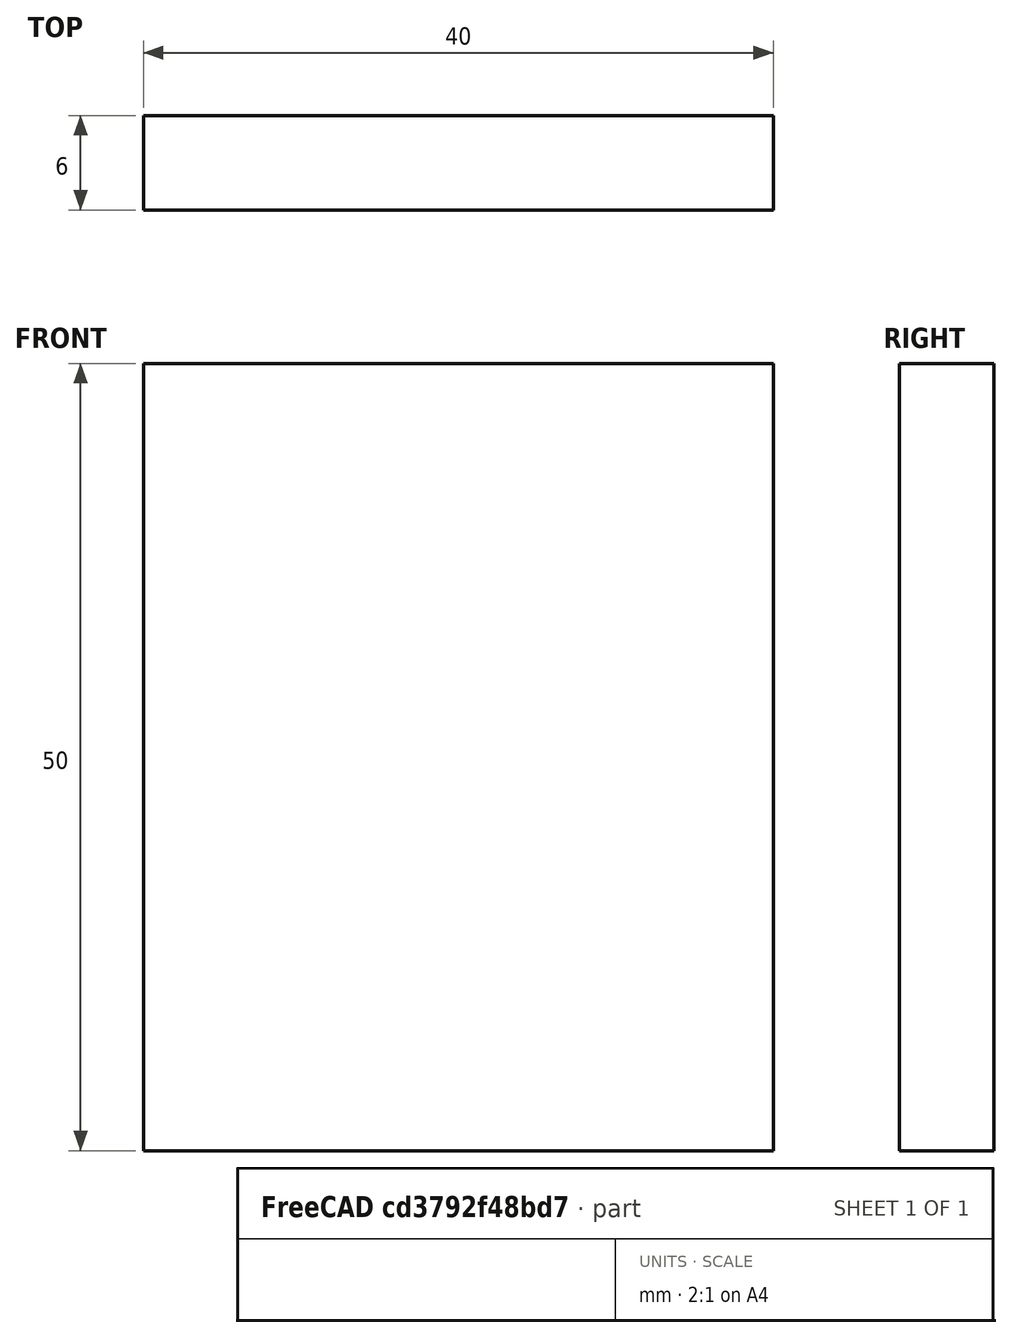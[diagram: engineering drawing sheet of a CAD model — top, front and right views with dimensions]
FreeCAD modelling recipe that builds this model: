
FCSTD DOCUMENT  (FreeCAD 0.15R4671 (Git))
Label: Flat Bar 40x6 EN10058 S235JR
License: All rights reserved
LicenseURL: http://en.wikipedia.org/wiki/All_rights_reserved
objects: Sketcher::SketchObject×1, Part::Extrusion×1
note: 2 computed .brp shape members not serialized (recipe doc carries the construction recipe); baked Part::Feature solids carry a one-line shape summary decoded from their .brp

FEATURE [Sketcher::SketchObject] Sketch
  sketch-geometry (4):
    g0: LineSegment StartX=-20 StartY=-3 StartZ=0 EndX=20 EndY=-3 EndZ=0
    g1: LineSegment StartX=20 StartY=-3 StartZ=0 EndX=20 EndY=3 EndZ=0
    g2: LineSegment StartX=20 StartY=3 StartZ=0 EndX=-20 EndY=3 EndZ=0
    g3: LineSegment StartX=-20 StartY=3 StartZ=0 EndX=-20 EndY=-3 EndZ=0
  constraints (12):
    c: Coincident(g0,g1)
    c: Coincident(g1,g2)
    c: Coincident(g2,g3)
    c: Coincident(g3,g0)
    c: Horizontal(g0)
    c: Horizontal(g2)
    c: Vertical(g1)
    c: Vertical(g3)
    c: Symmetric(g1,g2,g-2)
    c: Symmetric(g0,g1,g-1)
    c: DistanceY(g1) = 6
    c: DistanceX(g0) = 40
FEATURE [Part::Extrusion] Extrude  label="Flat Bar 40x6 EN10058 S235JR"
  Base = -> Sketch
  Dir = (0,0,50)
  Solid = true
